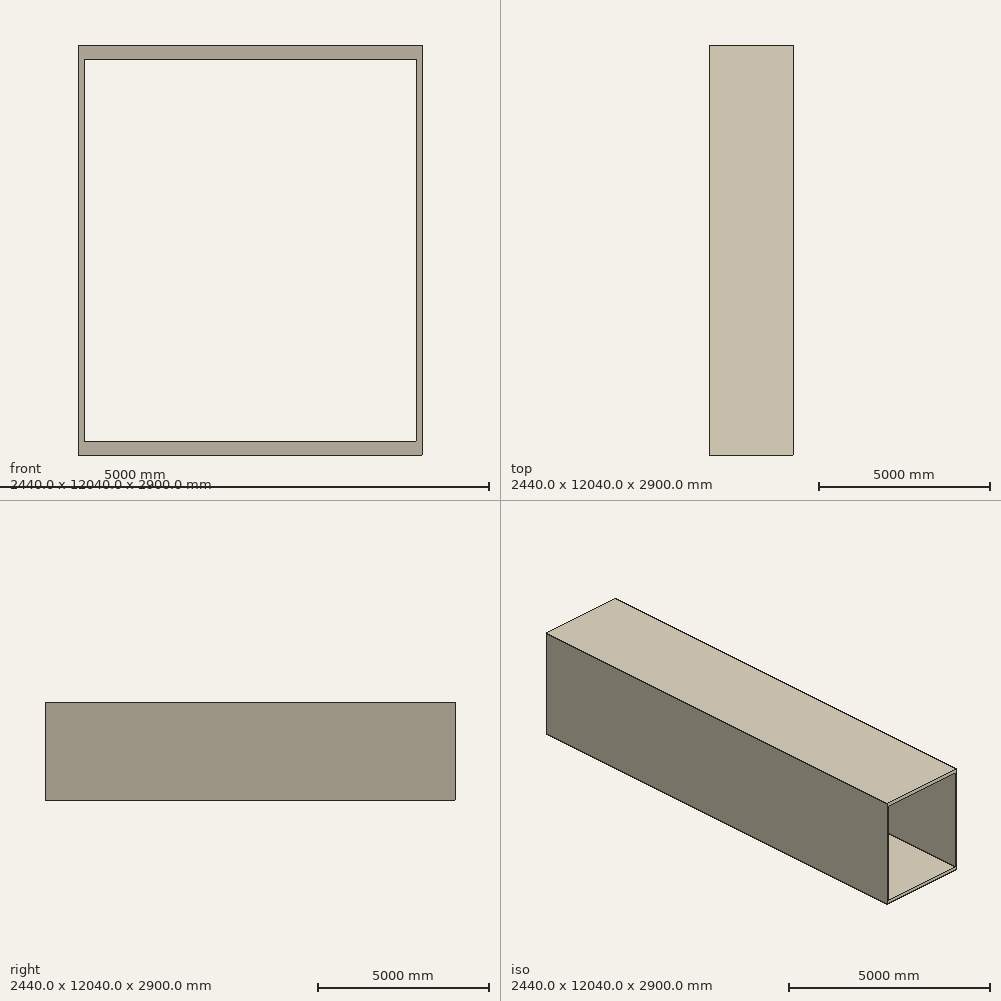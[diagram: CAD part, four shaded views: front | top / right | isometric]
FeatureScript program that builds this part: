
annotation { "Feature Type Name" : "Feature", "Feature Type Description" : "" }
export const myFeature = defineFeature(function(context is Context, id is Id, definition is map)
    precondition{}
    {
        {
            var Q0;
            Q0=qCreatedBy(makeId("Front.planeOp"),FACE);
            var sketch = newSketch(context, id + "F0", { "sketchPlane" : qUnion([Q0])});
            skLineSegment(sketch, "E0.bottom", {"start": v(-1220, 1450) * mm, "end": v(1220, 1450) * mm});
            skLineSegment(sketch, "E0.top", {"start": v(-1220, -1450) * mm, "end": v(1220, -1450) * mm});
            skLineSegment(sketch, "E0.left", {"start": v(-1220, 1450) * mm, "end": v(-1220, -1450) * mm});
            skLineSegment(sketch, "E0.right", {"start": v(1220, 1450) * mm, "end": v(1220, -1450) * mm});
            skLineSegment(sketch, "E1.bottom", {"start": v(-1175, 1350) * mm, "end": v(1175, 1350) * mm});
            skLineSegment(sketch, "E1.top", {"start": v(-1175, -1350) * mm, "end": v(1175, -1350) * mm});
            skLineSegment(sketch, "E1.left", {"start": v(-1175, 1350) * mm, "end": v(-1175, -1350) * mm});
            skLineSegment(sketch, "E1.right", {"start": v(1175, 1350) * mm, "end": v(1175, -1350) * mm});
            skSolve(sketch);
        }
        {
            var Q0;
            Q0 = qSketchRegion(id + "F0", true);
            extrude(context, id + "F1", {"entities" : qUnion([Q0]), "depth" : 12040 * mm, "offsetDistance" : 25 * mm});
        }
    });
